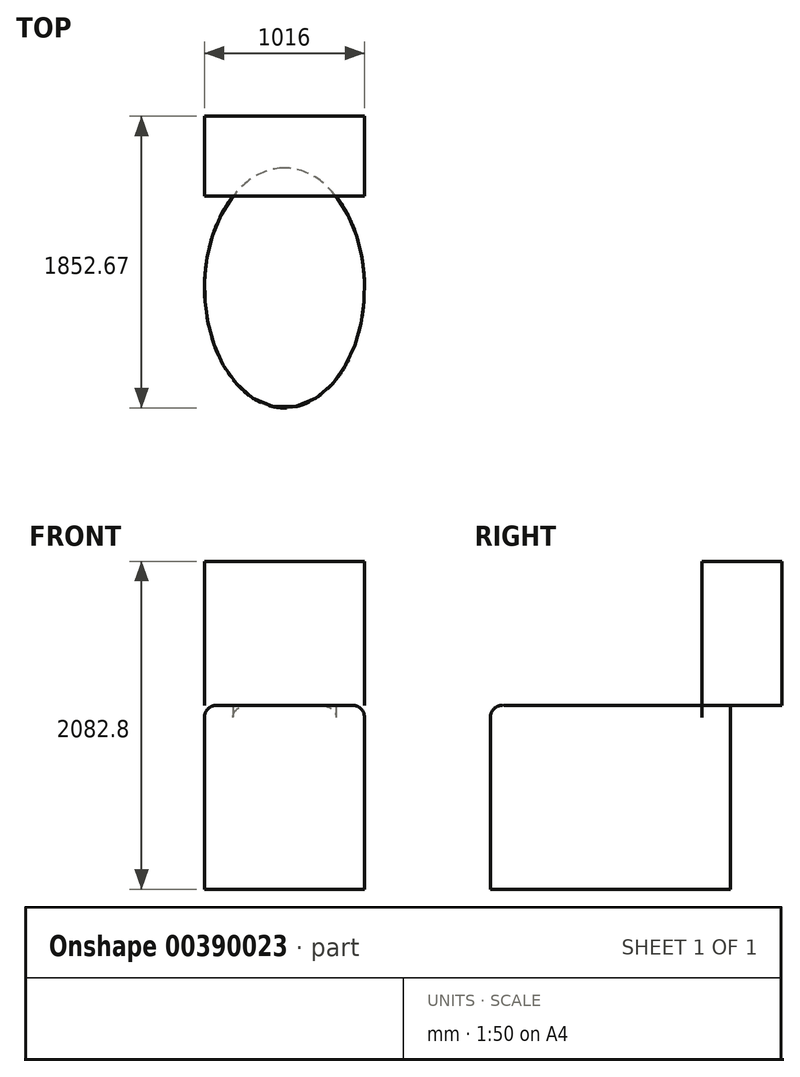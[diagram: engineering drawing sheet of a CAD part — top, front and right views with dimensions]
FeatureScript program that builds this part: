
annotation { "Feature Type Name" : "Feature", "Feature Type Description" : "" }
export const myFeature = defineFeature(function(context is Context, id is Id, definition is map)
    precondition{}
    {
        {
            var Q0;
            Q0=qCreatedBy(makeId("Top.planeOp"),FACE);
            var sketch = newSketch(context, id + "F0", { "sketchPlane" : qUnion([Q0])});
            skEllipse(sketch, "E0", {"center": v(0, 0) * mm, "majorRadius": 762 * mm, "minorRadius": 508 * mm, "majorAxis": v(0, 1)});
            skSolve(sketch);
        }
        {
            var Q0;
            Q0 = qSketchRegion(id + "F0", true);
            extrude(context, id + "F1", {"entities" : qUnion([Q0]), "depth" : 1168.4 * mm});
        }
        {
            var Q0;
            Q0=makeQuery(id+"F1.opExtrude","CAP_FACE",FACE,{"disambiguationData":[OSD([sQuery(id+"F0.wireOp",EDGE,"E0")])],"isStart":false});
            var sketch = newSketch(context, id + "F2", { "sketchPlane" : qUnion([Q0])});
            skLineSegment(sketch, "E1.bottom", {"start": v(-508, 1090.67) * mm, "end": v(508, 1090.67) * mm});
            skLineSegment(sketch, "E1.top", {"start": v(-508, 582.67) * mm, "end": v(508, 582.67) * mm});
            skLineSegment(sketch, "E1.left", {"start": v(-508, 1090.67) * mm, "end": v(-508, 582.67) * mm});
            skLineSegment(sketch, "E1.right", {"start": v(508, 1090.67) * mm, "end": v(508, 582.67) * mm});
            skSolve(sketch);
        }
        {
            var Q0;
            Q0 = qSketchRegion(id + "F2", true);
            extrude(context, id + "F3", {"entities" : qUnion([Q0]), "operationType" : NewBodyOperationType.ADD, "depth" : 914.4 * mm});
        }
        {
            var Q0;
            {var subQ0=sQuery(id+"F0.wireOp",EDGE,"E0");Q0=makeQuery(id+"F3.boolean.opBoolean","SPLIT",EDGE,{"disambiguationData":[topologyDisambiguationEdgeConnected([makeQuery(id+"F3.opExtrude","CAP_FACE",FACE,{"disambiguationData":[OSD([sQuery(id+"F2.wireOp",EDGE,"E1.bottom"),sQuery(id+"F2.wireOp",EDGE,"E1.top"),sQuery(id+"F2.wireOp",EDGE,"E1.left"),sQuery(id+"F2.wireOp",EDGE,"E1.right")])],"isStart":true})])],"derivedFrom":makeQuery(id+"F1.opExtrude","CAP_EDGE",EDGE,{"disambiguationData":[OSD([subQ0])],"isStart":false})});}
            fillet(context, id + "F4", {"entities" : qUnion([Q0]), "radius" : 76.2 * mm, "tangentPropagation" : true, "allowEdgeOverflow" : false});
        }
    });
